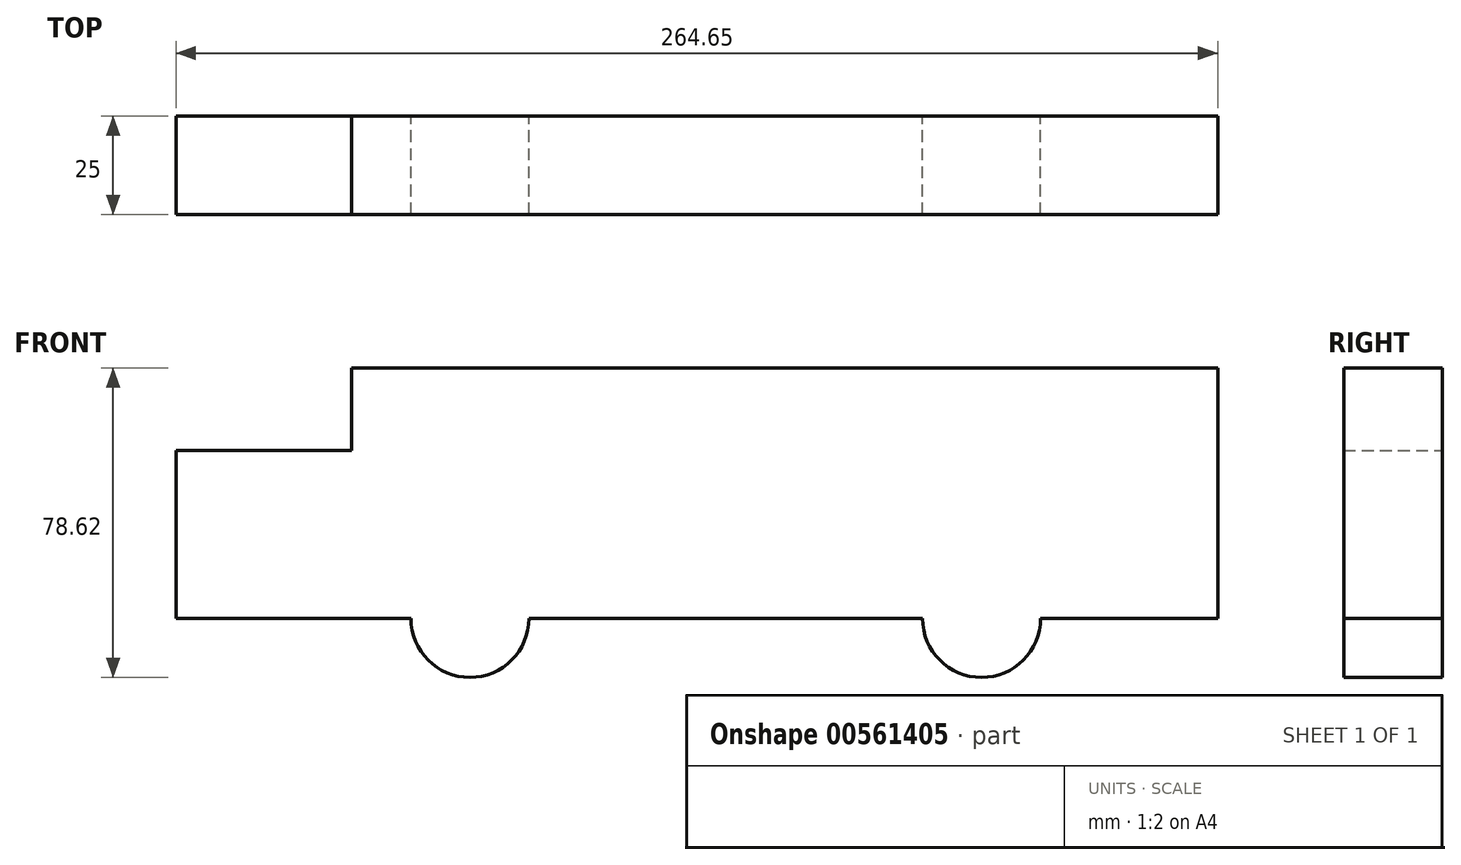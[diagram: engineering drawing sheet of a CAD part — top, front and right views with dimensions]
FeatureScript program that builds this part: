
annotation { "Feature Type Name" : "Feature", "Feature Type Description" : "" }
export const myFeature = defineFeature(function(context is Context, id is Id, definition is map)
    precondition{}
    {
        {
            var Q0;
            Q0=qCreatedBy(makeId("Front.planeOp"),FACE);
            var sketch = newSketch(context, id + "F0", { "sketchPlane" : qUnion([Q0])});
            skLineSegment(sketch, "E0.bottom", {"start": v(0, 0) * mm, "end": v(-220, 0) * mm});
            skLineSegment(sketch, "E0.top", {"start": v(0, -63.62) * mm, "end": v(-220, -63.62) * mm});
            skLineSegment(sketch, "E0.left", {"start": v(0, 0) * mm, "end": v(0, -63.62) * mm});
            skLineSegment(sketch, "E0.right", {"start": v(-220, 0) * mm, "end": v(-220, -63.62) * mm});
            skCircle(sketch, "E1", {"center": v(-190, -63.62) * mm, "radius": 15 * mm});
            skCircle(sketch, "E2", {"center": v(-60, -63.62) * mm, "radius": 15 * mm});
            skLineSegment(sketch, "E3", {"start": v(-220, -63.62) * mm, "end": v(-264.65, -63.62) * mm});
            skLineSegment(sketch, "E4", {"start": v(-264.65, -63.62) * mm, "end": v(-264.65, -20.97) * mm});
            skLineSegment(sketch, "E5", {"start": v(-264.65, -20.97) * mm, "end": v(-220, -20.97) * mm});
            skSolve(sketch);
        }
        {
            var Q0;
            Q0 = qSketchRegion(id + "F0", true);
            extrude(context, id + "F1", {"entities" : qUnion([Q0]), "depth" : 25 * mm, "offsetDistance" : 25 * mm});
        }
    });
